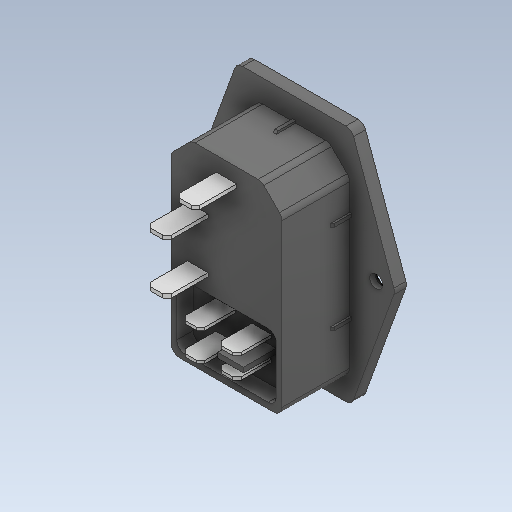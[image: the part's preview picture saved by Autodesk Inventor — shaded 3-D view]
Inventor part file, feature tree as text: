
AUTODESK INVENTOR PART (.ipt)
format: ipt  version: 2020 (Build 240168000, 168)  size: 260,096 bytes
history: native  units: in
note: dims shown in document units (in); Inventor stores cm internally (conversion verified against a paired STEP export)
features: chamfer x1
ambient origin geometry x8: Origin, YZ Plane, XZ Plane, XY Plane, X Axis, Y Axis, Z Axis, Center Point
bodies: Solid1 (feature_tree)
feature tree (1):
  chamfer  "Chamfer4"  [1 undecoded]
note: 1 required parameter value undecoded (feature->parameter linkage not recoverable at this tier; creation-order binding heuristic only, values carry confidence <= 0.55)
